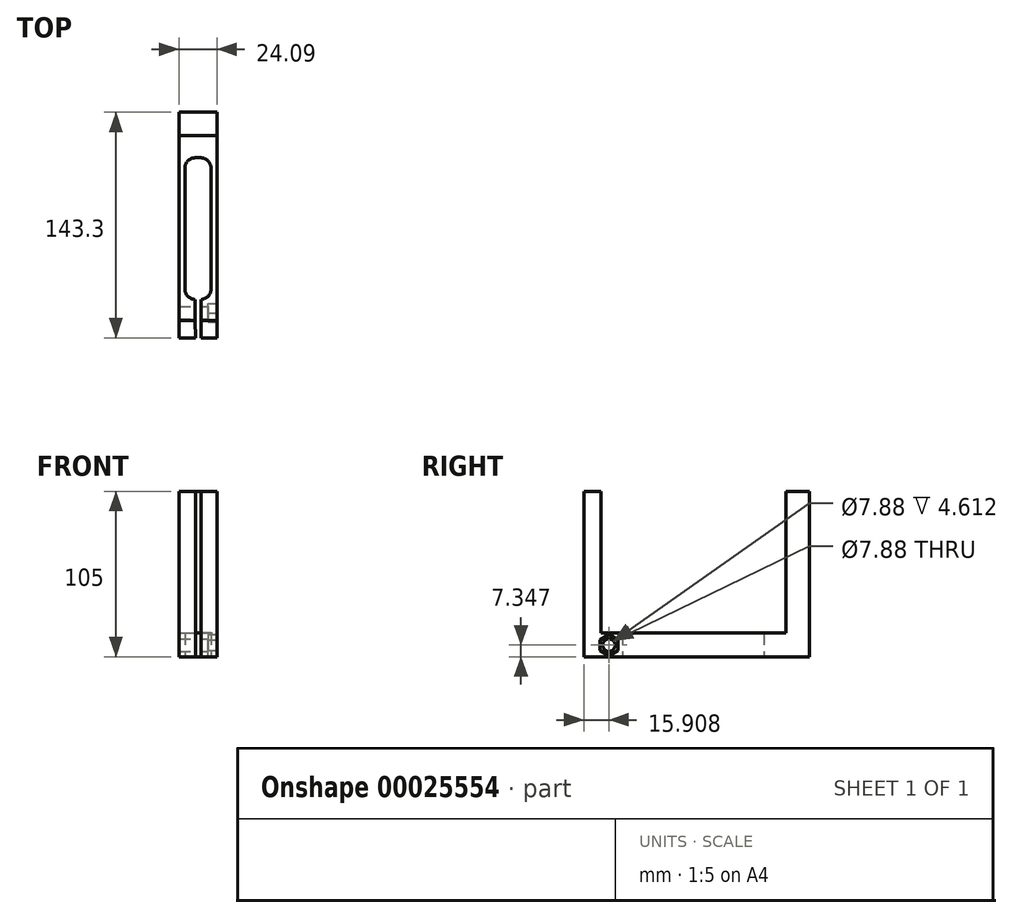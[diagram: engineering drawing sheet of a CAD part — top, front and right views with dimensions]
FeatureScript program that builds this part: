
annotation { "Feature Type Name" : "Feature", "Feature Type Description" : "" }
export const myFeature = defineFeature(function(context is Context, id is Id, definition is map)
    precondition{}
    {
        {
            var Q0;
            Q0=qCreatedBy(makeId("Top.planeOp"),FACE);
            var sketch = newSketch(context, id + "F0", { "sketchPlane" : qUnion([Q0])});
            skLineSegment(sketch, "E0.bottom", {"start": v(-10.8, 30.74) * mm, "end": v(-7.1, 30.74) * mm});
            skLineSegment(sketch, "E0.top", {"start": v(-10.8, -59.26) * mm, "end": v(-7.1, -59.26) * mm});
            skLineSegment(sketch, "E0.left", {"start": v(-17.15, 24.4) * mm, "end": v(-17.15, -52.9) * mm});
            skLineSegment(sketch, "E0.right", {"start": v(-0.75, 24.4) * mm, "end": v(-0.75, -52.9) * mm});
            skPoint(sketch, "E1.visualSharp", {"position": v(-17.15, 30.74) * mm});
            skArc(sketch, "E1.filletArc", {"start": v(-10.8, 30.74) * mm, "mid": v(-15.3, 28.88) * mm, "end": v(-17.15, 24.4) * mm});
            skPoint(sketch, "E2.visualSharp", {"position": v(-0.75, 30.74) * mm});
            skArc(sketch, "E2.filletArc", {"start": v(-0.75, 24.4) * mm, "mid": v(-2.61, 28.88) * mm, "end": v(-7.1, 30.74) * mm});
            skPoint(sketch, "E3.visualSharp", {"position": v(-17.15, -59.26) * mm});
            skArc(sketch, "E3.filletArc", {"start": v(-17.15, -52.9) * mm, "mid": v(-15.3, -57.4) * mm, "end": v(-10.8, -59.26) * mm});
            skPoint(sketch, "E4.visualSharp", {"position": v(-0.75, -59.26) * mm});
            skArc(sketch, "E4.filletArc", {"start": v(-7.1, -59.26) * mm, "mid": v(-2.61, -57.4) * mm, "end": v(-0.75, -52.9) * mm});
            skLineSegment(sketch, "E5", {"start": v(3.01, -83.65) * mm, "end": v(3.01, 59.65) * mm});
            skLineSegment(sketch, "E6", {"start": v(3.01, 59.65) * mm, "end": v(-21.08, 59.65) * mm});
            skLineSegment(sketch, "E7", {"start": v(-21.08, 59.65) * mm, "end": v(-21.08, -83.65) * mm});
            skLineSegment(sketch, "E8", {"start": v(-21.08, -83.65) * mm, "end": v(-10.57, -83.65) * mm});
            skLineSegment(sketch, "E9", {"start": v(-10.57, -83.65) * mm, "end": v(-10.8, -59.26) * mm});
            skLineSegment(sketch, "E10", {"start": v(-7.1, -59.26) * mm, "end": v(-7.1, -83.65) * mm});
            skLineSegment(sketch, "E11", {"start": v(-7.1, -83.65) * mm, "end": v(3.01, -83.65) * mm});
            skSolve(sketch);
        }
        {
            var Q0;
            Q0=makeQuery(id+"F0.imprint","IMPRINT",FACE,{"disambiguationData":[TD([[makeQuery(id+"F0.imprint","IMPRINT",EDGE,{"derivedFrom":sQuery(id+"F0.wireOp",EDGE,"E0.bottom")}),1.0]])]});
            extrude(context, id + "F1", {"entities" : qUnion([Q0]), "depth" : 15 * mm});
        }
        {
            var Q0;
            Q0=makeQuery(id+"F1.opExtrude","CAP_FACE",FACE,{"disambiguationData":[OSD([sQuery(id+"F0.wireOp",EDGE,"E0.bottom"),sQuery(id+"F0.wireOp",EDGE,"E0.left"),sQuery(id+"F0.wireOp",EDGE,"E0.right"),sQuery(id+"F0.wireOp",EDGE,"E1.filletArc"),sQuery(id+"F0.wireOp",EDGE,"E2.filletArc"),sQuery(id+"F0.wireOp",EDGE,"E3.filletArc"),sQuery(id+"F0.wireOp",EDGE,"E4.filletArc"),sQuery(id+"F0.wireOp",EDGE,"E5"),sQuery(id+"F0.wireOp",EDGE,"E6"),sQuery(id+"F0.wireOp",EDGE,"E7"),sQuery(id+"F0.wireOp",EDGE,"E8"),sQuery(id+"F0.wireOp",EDGE,"E9"),sQuery(id+"F0.wireOp",EDGE,"E10"),sQuery(id+"F0.wireOp",EDGE,"E11")])],"isStart":false});
            var sketch = newSketch(context, id + "F2", { "sketchPlane" : qUnion([Q0])});
            skLineSegment(sketch, "E12.bottom", {"start": v(-21.08, 59.65) * mm, "end": v(3.01, 59.65) * mm});
            skLineSegment(sketch, "E12.top", {"start": v(-21.08, 44.72) * mm, "end": v(3.01, 44.72) * mm});
            skLineSegment(sketch, "E12.left", {"start": v(-21.08, 59.65) * mm, "end": v(-21.08, 44.72) * mm});
            skLineSegment(sketch, "E12.right", {"start": v(3.01, 59.65) * mm, "end": v(3.01, 44.72) * mm});
            skLineSegment(sketch, "E13.bottom", {"start": v(-21.08, -72.7) * mm, "end": v(-10.57, -72.7) * mm});
            skLineSegment(sketch, "E13.top", {"start": v(-21.08, -83.65) * mm, "end": v(-10.57, -83.65) * mm});
            skLineSegment(sketch, "E13.left", {"start": v(-21.08, -72.7) * mm, "end": v(-21.08, -83.65) * mm});
            skLineSegment(sketch, "E13.right", {"start": v(-10.57, -72.7) * mm, "end": v(-10.57, -83.65) * mm});
            skLineSegment(sketch, "E14.bottom", {"start": v(-7.1, -72.7) * mm, "end": v(3.01, -72.7) * mm});
            skLineSegment(sketch, "E14.top", {"start": v(-7.1, -83.65) * mm, "end": v(3.01, -83.65) * mm});
            skLineSegment(sketch, "E14.left", {"start": v(-7.1, -72.7) * mm, "end": v(-7.1, -83.65) * mm});
            skLineSegment(sketch, "E14.right", {"start": v(3.01, -72.7) * mm, "end": v(3.01, -83.65) * mm});
            skSolve(sketch);
        }
        {
            var Q0;
            Q0=makeQuery(id+"F2.imprint","IMPRINT",FACE,{"disambiguationData":[TD([[makeQuery(id+"F2.imprint","IMPRINT",EDGE,{"derivedFrom":sQuery(id+"F2.wireOp",EDGE,"E12.bottom")}),1.0]])]});
            var Q1;
            {var subQ3=sQuery(id+"F2.wireOp",EDGE,"E13.top");Q1=makeQuery(id+"F2.imprint","IMPRINT",FACE,{"disambiguationData":[TD([[makeQuery(id+"F2.imprint","IMPRINT",EDGE,{"derivedFrom":subQ3}),1.0]])]});}
            var Q2;
            Q2=makeQuery(id+"F2.imprint","IMPRINT",FACE,{"disambiguationData":[TD([[makeQuery(id+"F2.imprint","IMPRINT",EDGE,{"derivedFrom":sQuery(id+"F2.wireOp",EDGE,"E14.bottom")}),-1.0]])]});
            extrude(context, id + "F3", {"entities" : qUnion([Q0, Q1, Q2]), "operationType" : NewBodyOperationType.ADD, "depth" : 90 * mm});
        }
        {
            var Q0;
            Q0=makeQuery(id+"F3.boolean.opBoolean","MERGE",FACE,{"derivedFrom":[makeQuery(id+"F1.opExtrude","SWEPT_FACE",FACE,{"disambiguationData":[OSD([sQuery(id+"F0.wireOp",EDGE,"E7")])]}),makeQuery(id+"F3.opExtrude","SWEPT_FACE",FACE,{"disambiguationData":[OSD([sQuery(id+"F2.wireOp",EDGE,"E12.left")])]}),makeQuery(id+"F3.opExtrude","SWEPT_FACE",FACE,{"disambiguationData":[OSD([sQuery(id+"F2.wireOp",EDGE,"E13.left")])]})]});
            var sketch = newSketch(context, id + "F4", { "sketchPlane" : qUnion([Q0])});
            skCircle(sketch, "E15", {"center": v(67.74, 7.35) * mm, "radius": 3.94 * mm});
            skSolve(sketch);
        }
        {
            var Q0;
            Q0=makeQuery(id+"F4.imprint","IMPRINT",FACE,{"disambiguationData":[TD([[makeQuery(id+"F4.imprint","IMPRINT",EDGE,{"derivedFrom":sQuery(id+"F4.wireOp",EDGE,"E15")}),1.0]])]});
            extrude(context, id + "F5", {"entities" : qUnion([Q0]), "operationType" : NewBodyOperationType.REMOVE, "endBound" : BoundingType.THROUGH_ALL, "depth" : 25 * mm, "hasSecondDirection" : true, "secondDirectionOppositeDirection" : true, "secondDirectionDepth" : 25 * mm});
        }
        {
            var Q0;
            Q0=makeQuery(id+"F3.boolean.opBoolean","MERGE",FACE,{"derivedFrom":[makeQuery(id+"F1.opExtrude","SWEPT_FACE",FACE,{"disambiguationData":[OSD([sQuery(id+"F0.wireOp",EDGE,"E5")])]}),makeQuery(id+"F3.opExtrude","SWEPT_FACE",FACE,{"disambiguationData":[OSD([sQuery(id+"F2.wireOp",EDGE,"E12.right")])]}),makeQuery(id+"F3.opExtrude","SWEPT_FACE",FACE,{"disambiguationData":[OSD([sQuery(id+"F2.wireOp",EDGE,"E14.right")])]})]});
            var sketch = newSketch(context, id + "F6", { "sketchPlane" : qUnion([Q0])});
            skCircle(sketch, "E16.cCircle", {"center": v(-67.74, 7.35) * mm, "radius": 5.8 * mm, "construction": true});
            skLineSegment(sketch, "E16.0", {"start": v(-61.94, 10.7) * mm, "end": v(-61.94, 4) * mm});
            skLineSegment(sketch, "E16.1", {"start": v(-61.94, 4) * mm, "end": v(-67.74, 0.65) * mm});
            skLineSegment(sketch, "E16.2", {"start": v(-67.74, 0.65) * mm, "end": v(-73.54, 4) * mm});
            skLineSegment(sketch, "E16.3", {"start": v(-73.54, 4) * mm, "end": v(-73.54, 10.7) * mm});
            skLineSegment(sketch, "E16.4", {"start": v(-73.54, 10.7) * mm, "end": v(-67.74, 14.05) * mm});
            skLineSegment(sketch, "E16.5", {"start": v(-67.74, 14.05) * mm, "end": v(-61.94, 10.7) * mm});
            skPoint(sketch, "E16.0.midPoint", {"position": v(-61.94, 7.35) * mm});
            skSolve(sketch);
        }
        {
            var Q0;
            Q0 = qSketchRegion(id + "F6", true);
            extrude(context, id + "F7", {"entities" : qUnion([Q0]), "operationType" : NewBodyOperationType.REMOVE, "oppositeDirection" : true, "depth" : 5.5 * mm});
        }
    });
